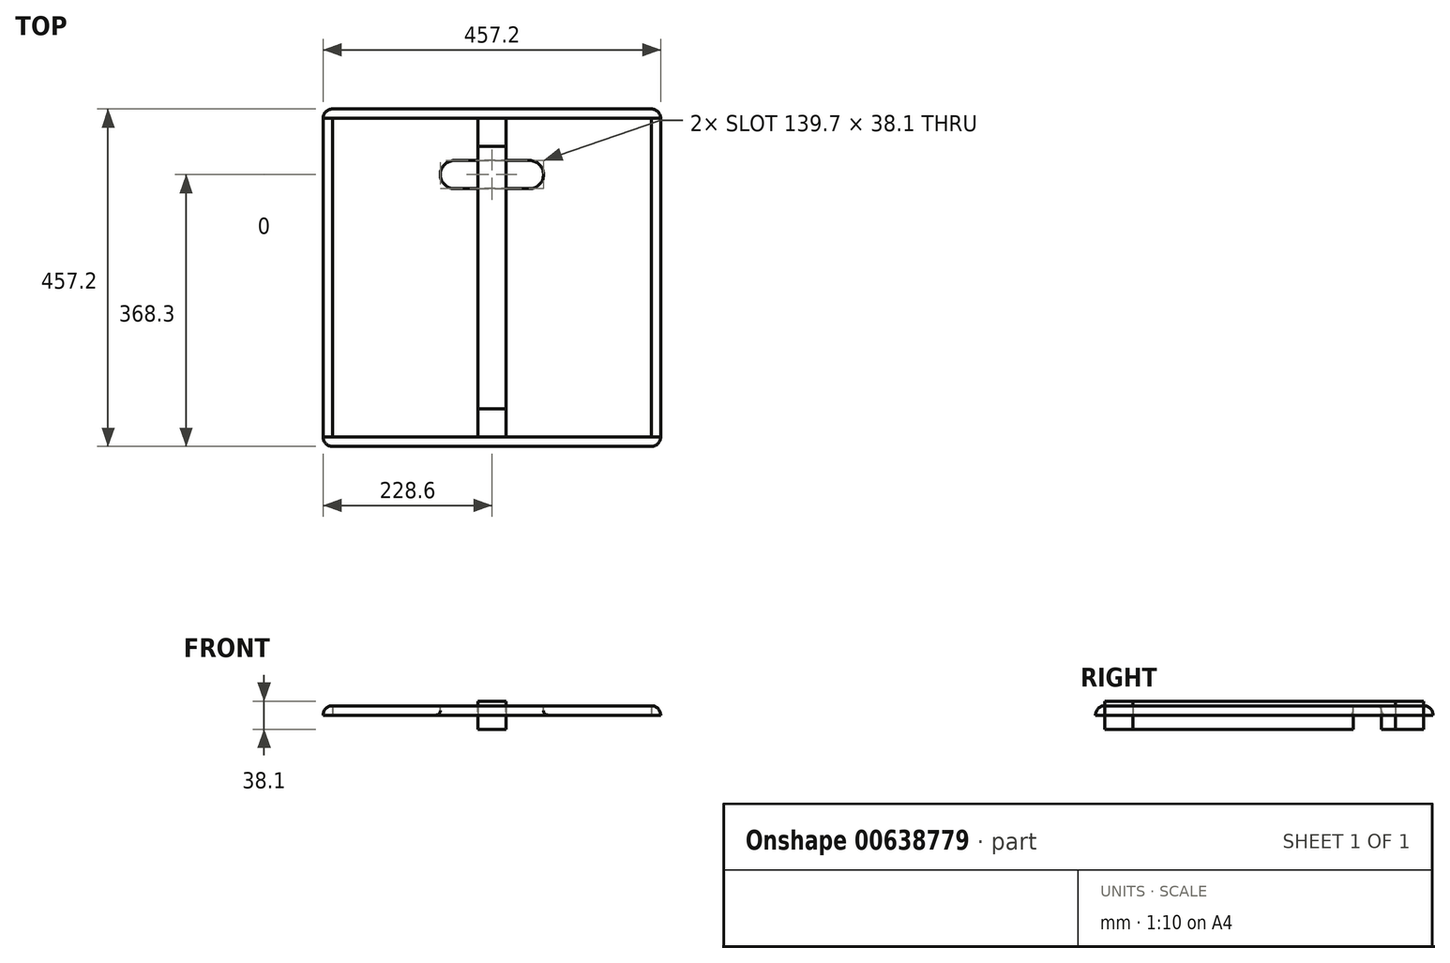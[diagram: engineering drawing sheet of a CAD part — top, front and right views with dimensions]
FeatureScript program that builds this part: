
annotation { "Feature Type Name" : "Feature", "Feature Type Description" : "" }
export const myFeature = defineFeature(function(context is Context, id is Id, definition is map)
    precondition{}
    {
        {
            var Q0;
            Q0=qCreatedBy(makeId("Top.planeOp"),FACE);
            var sketch = newSketch(context, id + "F0", { "sketchPlane" : qUnion([Q0])});
            skLineSegment(sketch, "E0.bottom", {"start": v(228.6, 228.6) * mm, "end": v(-228.6, 228.6) * mm});
            skLineSegment(sketch, "E0.top", {"start": v(228.6, -228.6) * mm, "end": v(-228.6, -228.6) * mm});
            skLineSegment(sketch, "E0.left", {"start": v(228.6, 228.6) * mm, "end": v(228.6, -228.6) * mm});
            skLineSegment(sketch, "E0.right", {"start": v(-228.6, 228.6) * mm, "end": v(-228.6, -228.6) * mm});
            skPoint(sketch, "E0.middle", {"position": v(0, 0) * mm});
            skSolve(sketch);
        }
        {
            var Q0;
            Q0=makeQuery(id+"F0.imprint","IMPRINT",FACE,{"disambiguationData":[TD([[makeQuery(id+"F0.imprint","IMPRINT",EDGE,{"derivedFrom":sQuery(id+"F0.wireOp",EDGE,"E0.bottom")}),1.0]])]});
            extrude(context, id + "F1", {"entities" : qUnion([Q0]), "depth" : 12.7 * mm, "offsetDistance" : 25.4 * mm});
        }
        {
            var Q0;
            Q0=makeQuery(id+"F1.opExtrude","CAP_EDGE",EDGE,{"disambiguationData":[OSD([sQuery(id+"F0.wireOp",EDGE,"E0.right")])],"isStart":false});
            var Q1;
            Q1=makeQuery(id+"F1.opExtrude","CAP_EDGE",EDGE,{"disambiguationData":[OSD([sQuery(id+"F0.wireOp",EDGE,"E0.top")])],"isStart":false});
            var Q2;
            Q2=makeQuery(id+"F1.opExtrude","CAP_EDGE",EDGE,{"disambiguationData":[OSD([sQuery(id+"F0.wireOp",EDGE,"E0.left")])],"isStart":false});
            var Q3;
            Q3=makeQuery(id+"F1.opExtrude","CAP_EDGE",EDGE,{"disambiguationData":[OSD([sQuery(id+"F0.wireOp",EDGE,"E0.bottom")])],"isStart":false});
            var Q4;
            Q4=makeQuery(id+"F1.opExtrude","SWEPT_EDGE",EDGE,{"disambiguationData":[OSD([sQuery(id+"F0.wireOp",EDGE,"E0.top"),sQuery(id+"F0.wireOp",EDGE,"E0.left")])]});
            var Q5;
            Q5=makeQuery(id+"F1.opExtrude","SWEPT_EDGE",EDGE,{"disambiguationData":[OSD([sQuery(id+"F0.wireOp",EDGE,"E0.top"),sQuery(id+"F0.wireOp",EDGE,"E0.right")])]});
            var Q6;
            Q6=makeQuery(id+"F1.opExtrude","SWEPT_EDGE",EDGE,{"disambiguationData":[OSD([sQuery(id+"F0.wireOp",EDGE,"E0.bottom"),sQuery(id+"F0.wireOp",EDGE,"E0.right")])]});
            var Q7;
            Q7=makeQuery(id+"F1.opExtrude","SWEPT_EDGE",EDGE,{"disambiguationData":[OSD([sQuery(id+"F0.wireOp",EDGE,"E0.bottom"),sQuery(id+"F0.wireOp",EDGE,"E0.left")])]});
            fillet(context, id + "F2", {"entities" : qUnion([Q0, Q1, Q2, Q3, Q4, Q5, Q6, Q7]), "radius" : 12.7 * mm, "tangentPropagation" : true, "allowEdgeOverflow" : false});
        }
        {
            var Q0;
            Q0=qCreatedBy(makeId("Top.planeOp"),FACE);
            var sketch = newSketch(context, id + "F3", { "sketchPlane" : qUnion([Q0])});
            skLineSegment(sketch, "E1.bottom", {"start": v(-228.6, 215.9) * mm, "end": v(228.6, 215.9) * mm});
            skLineSegment(sketch, "E1.top", {"start": v(-228.6, -215.9) * mm, "end": v(228.6, -215.9) * mm});
            skLineSegment(sketch, "E1.left", {"start": v(-228.6, 215.9) * mm, "end": v(-228.6, -215.9) * mm});
            skLineSegment(sketch, "E1.right", {"start": v(228.6, 215.9) * mm, "end": v(228.6, -215.9) * mm});
            skPoint(sketch, "E1.middle", {"position": v(0, 0) * mm});
            skSolve(sketch);
        }
        {
            var Q0;
            Q0=makeQuery(id+"F3.imprint","IMPRINT",FACE,{"disambiguationData":[TD([[makeQuery(id+"F3.imprint","IMPRINT",EDGE,{"derivedFrom":sQuery(id+"F3.wireOp",EDGE,"E1.bottom")}),-1.0]])]});
            extrude(context, id + "F4", {"entities" : qUnion([Q0]), "depth" : 12.7 * mm, "offsetDistance" : 25.4 * mm});
        }
        {
            var Q0;
            Q0=makeQuery(id+"F4.opExtrude","CAP_EDGE",EDGE,{"disambiguationData":[OSD([sQuery(id+"F3.wireOp",EDGE,"E1.left")])],"isStart":false});
            var Q1;
            Q1=makeQuery(id+"F4.opExtrude","CAP_EDGE",EDGE,{"disambiguationData":[OSD([sQuery(id+"F3.wireOp",EDGE,"E1.right")])],"isStart":false});
            fillet(context, id + "F5", {"entities" : qUnion([Q0, Q1]), "radius" : 12.7 * mm, "tangentPropagation" : true, "allowEdgeOverflow" : false});
        }
        {
            var Q0;
            Q0=qCreatedBy(makeId("Top.planeOp"),FACE);
            var sketch = newSketch(context, id + "F6", { "sketchPlane" : qUnion([Q0])});
            skLineSegment(sketch, "E2.bottom", {"start": v(-215.9, 215.9) * mm, "end": v(215.9, 215.9) * mm});
            skLineSegment(sketch, "E2.top", {"start": v(-215.9, -215.9) * mm, "end": v(215.9, -215.9) * mm});
            skLineSegment(sketch, "E2.left", {"start": v(-215.9, 215.9) * mm, "end": v(-215.9, -215.9) * mm});
            skLineSegment(sketch, "E2.right", {"start": v(215.9, 215.9) * mm, "end": v(215.9, -215.9) * mm});
            skPoint(sketch, "E2.middle", {"position": v(0, 0) * mm});
            skSolve(sketch);
        }
        {
            var Q0;
            Q0=makeQuery(id+"F6.imprint","IMPRINT",FACE,{"disambiguationData":[TD([[makeQuery(id+"F6.imprint","IMPRINT",EDGE,{"derivedFrom":sQuery(id+"F6.wireOp",EDGE,"E2.bottom")}),-1.0]])]});
            extrude(context, id + "F7", {"entities" : qUnion([Q0]), "depth" : 12.7 * mm, "offsetDistance" : 25.4 * mm});
        }
        {
            var Q0;
            Q0=qCreatedBy(makeId("Front.planeOp"),FACE);
            var sketch = newSketch(context, id + "F8", { "sketchPlane" : qUnion([Q0])});
            skLineSegment(sketch, "E3.bottom", {"start": v(19.05, 19.05) * mm, "end": v(-19.05, 19.05) * mm});
            skLineSegment(sketch, "E3.top", {"start": v(19.05, -19.05) * mm, "end": v(-19.05, -19.05) * mm});
            skLineSegment(sketch, "E3.left", {"start": v(19.05, 19.05) * mm, "end": v(19.05, -19.05) * mm});
            skLineSegment(sketch, "E3.right", {"start": v(-19.05, 19.05) * mm, "end": v(-19.05, -19.05) * mm});
            skPoint(sketch, "E3.middle", {"position": v(0, 0) * mm});
            skSolve(sketch);
        }
        {
            var Q0;
            Q0=makeQuery(id+"F8.imprint","IMPRINT",FACE,{"disambiguationData":[TD([[makeQuery(id+"F8.imprint","IMPRINT",EDGE,{"derivedFrom":sQuery(id+"F8.wireOp",EDGE,"E3.bottom")}),1.0]])]});
            extrude(context, id + "F9", {"entities" : qUnion([Q0]), "endBound" : BoundingType.SYMMETRIC, "oppositeDirection" : true, "depth" : 431.8 * mm, "offsetDistance" : 25.4 * mm});
        }
        {
            var Q0;
            Q0=qCreatedBy(makeId("Front.planeOp"),FACE);
            var sketch = newSketch(context, id + "F10", { "sketchPlane" : qUnion([Q0])});
            skLineSegment(sketch, "E4.bottom", {"start": v(19.05, 19.05) * mm, "end": v(-19.05, 19.05) * mm});
            skLineSegment(sketch, "E4.top", {"start": v(19.05, -19.05) * mm, "end": v(-19.05, -19.05) * mm});
            skLineSegment(sketch, "E4.left", {"start": v(19.05, 19.05) * mm, "end": v(19.05, -19.05) * mm});
            skLineSegment(sketch, "E4.right", {"start": v(-19.05, 19.05) * mm, "end": v(-19.05, -19.05) * mm});
            skPoint(sketch, "E4.middle", {"position": v(0, 0) * mm});
            skSolve(sketch);
        }
        {
            var Q0;
            Q0=makeQuery(id+"F10.imprint","IMPRINT",FACE,{"disambiguationData":[TD([[makeQuery(id+"F10.imprint","IMPRINT",EDGE,{"derivedFrom":sQuery(id+"F10.wireOp",EDGE,"E4.bottom")}),1.0]])]});
            extrude(context, id + "F11", {"entities" : qUnion([Q0]), "endBound" : BoundingType.SYMMETRIC, "depth" : 355.6 * mm, "offsetDistance" : 25.4 * mm});
        }
        {
            var Q0;
            Q0=makeQuery(id+"F7.opExtrude","CAP_FACE",FACE,{"disambiguationData":[OSD([sQuery(id+"F6.wireOp",EDGE,"E2.bottom"),sQuery(id+"F6.wireOp",EDGE,"E2.top"),sQuery(id+"F6.wireOp",EDGE,"E2.left"),sQuery(id+"F6.wireOp",EDGE,"E2.right")])],"isStart":false});
            var sketch = newSketch(context, id + "F12", { "sketchPlane" : qUnion([Q0])});
            skLineSegment(sketch, "E5.bottom", {"start": v(50.8, 158.75) * mm, "end": v(-50.8, 158.75) * mm});
            skLineSegment(sketch, "E5.top", {"start": v(50.8, 120.65) * mm, "end": v(-50.8, 120.65) * mm});
            skPoint(sketch, "E5.middle", {"position": v(0, 139.7) * mm});
            skArc(sketch, "E6", {"start": v(50.8, 158.75) * mm, "mid": v(69.85, 139.7) * mm, "end": v(50.8, 120.65) * mm});
            skArc(sketch, "E7", {"start": v(-50.8, 158.75) * mm, "mid": v(-69.85, 139.7) * mm, "end": v(-50.8, 120.65) * mm});
            skSolve(sketch);
        }
        {
            var Q0;
            Q0=makeQuery(id+"F12.imprint","IMPRINT",FACE,{"disambiguationData":[TD([[makeQuery(id+"F12.imprint","IMPRINT",EDGE,{"derivedFrom":sQuery(id+"F12.wireOp",EDGE,"E5.bottom")}),1.0]])]});
            extrude(context, id + "F13", {"entities" : qUnion([Q0]), "operationType" : NewBodyOperationType.REMOVE, "endBound" : BoundingType.THROUGH_ALL, "oppositeDirection" : true, "depth" : 25.4 * mm, "offsetDistance" : 25.4 * mm});
        }
        {
            var Q0;
            Q0=makeQuery(id+"F13.boolean.opBoolean","COPY",EDGE,{"derivedFrom":makeQuery(id+"F13.opExtrude","CAP_EDGE",EDGE,{"disambiguationData":[OSD([sQuery(id+"F12.wireOp",EDGE,"E7")])],"isStart":true})});
            var Q1;
            Q1=makeQuery(id+"F13.boolean.opBoolean","COPY",EDGE,{"derivedFrom":makeQuery(id+"F13.opExtrude","CAP_EDGE",EDGE,{"disambiguationData":[OSD([sQuery(id+"F12.wireOp",EDGE,"E5.bottom")])],"isStart":true})});
            var Q2;
            Q2=makeQuery(id+"F13.boolean.opBoolean","INTERSECT",EDGE,{"derivedFrom":[makeQuery(id+"F7.opExtrude","CAP_FACE",FACE,{"disambiguationData":[OSD([sQuery(id+"F6.wireOp",EDGE,"E2.bottom"),sQuery(id+"F6.wireOp",EDGE,"E2.top"),sQuery(id+"F6.wireOp",EDGE,"E2.left"),sQuery(id+"F6.wireOp",EDGE,"E2.right")])],"isStart":true}),makeQuery(id+"F13.opExtrude","SWEPT_FACE",FACE,{"disambiguationData":[OSD([sQuery(id+"F12.wireOp",EDGE,"E5.top")])]})]});
            fillet(context, id + "F14", {"entities" : qUnion([Q0, Q1, Q2]), "radius" : 6.35 * mm, "tangentPropagation" : true, "allowEdgeOverflow" : false});
        }
    });
